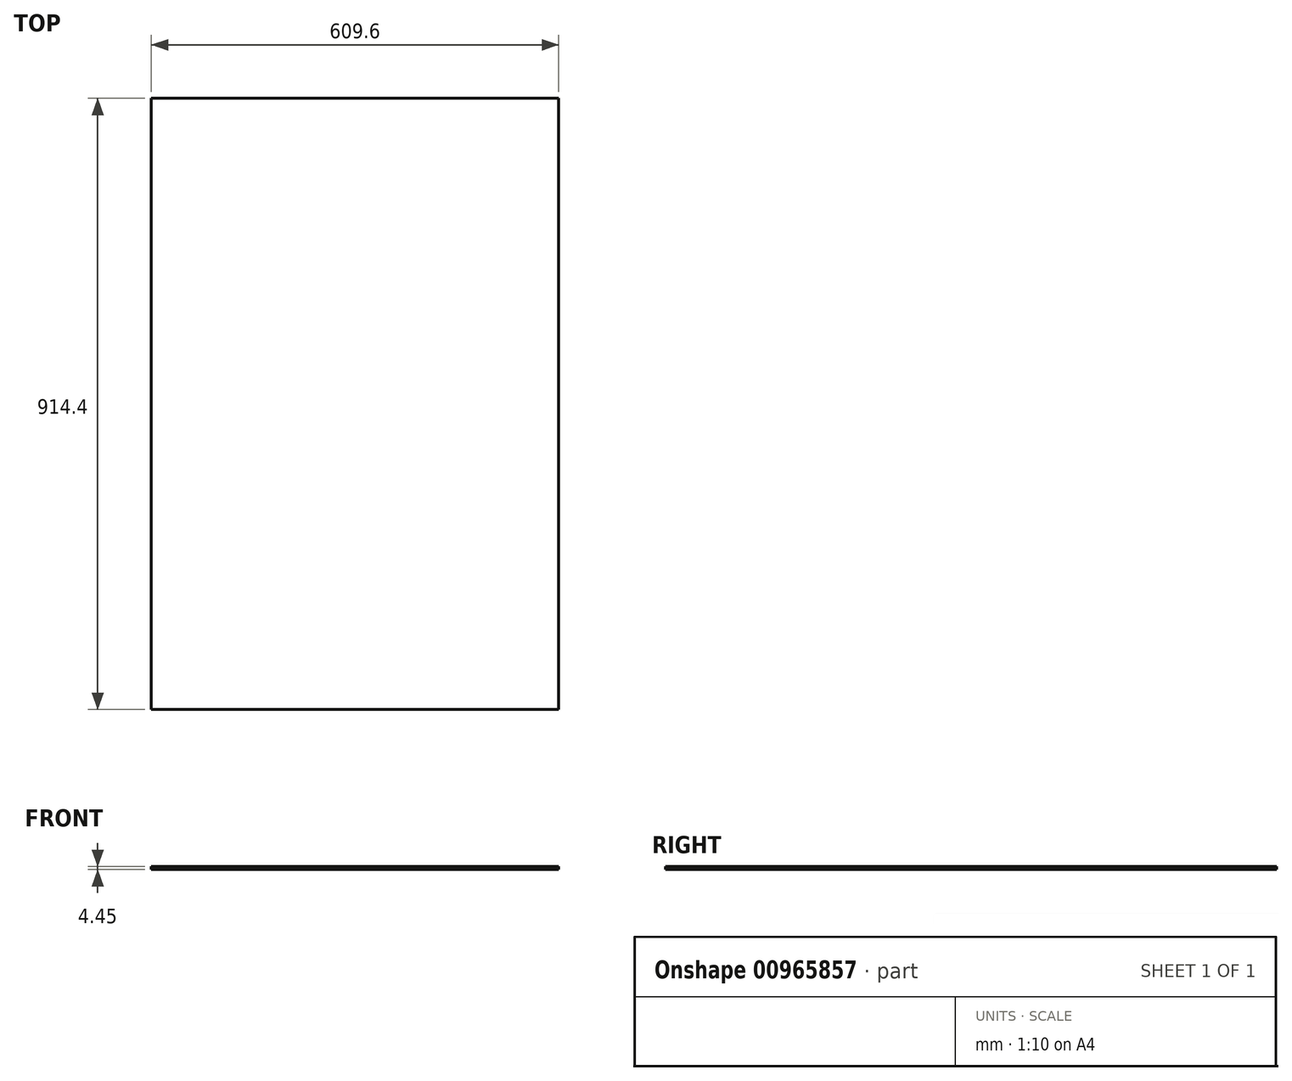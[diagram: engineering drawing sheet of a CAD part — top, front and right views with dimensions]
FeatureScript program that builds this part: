
annotation { "Feature Type Name" : "Feature", "Feature Type Description" : "" }
export const myFeature = defineFeature(function(context is Context, id is Id, definition is map)
    precondition{}
    {
        {
            var Q0;
            Q0=qCreatedBy(makeId("Top.planeOp"),FACE);
            var sketch = newSketch(context, id + "F0", { "sketchPlane" : qUnion([Q0])});
            skLineSegment(sketch, "E0.bottom", {"start": v(304.8, -457.2) * mm, "end": v(-304.8, -457.2) * mm});
            skLineSegment(sketch, "E0.top", {"start": v(304.8, 457.2) * mm, "end": v(-304.8, 457.2) * mm});
            skLineSegment(sketch, "E0.left", {"start": v(304.8, -457.2) * mm, "end": v(304.8, 457.2) * mm});
            skLineSegment(sketch, "E0.right", {"start": v(-304.8, -457.2) * mm, "end": v(-304.8, 457.2) * mm});
            skPoint(sketch, "E0.middle", {"position": v(0, 0) * mm});
            skSolve(sketch);
        }
        {
            var Q0;
            Q0 = qSketchRegion(id + "F0", true);
            extrude(context, id + "F1", {"entities" : qUnion([Q0]), "depth" : 4.45 * mm, "offsetDistance" : 25.4 * mm});
        }
    });
